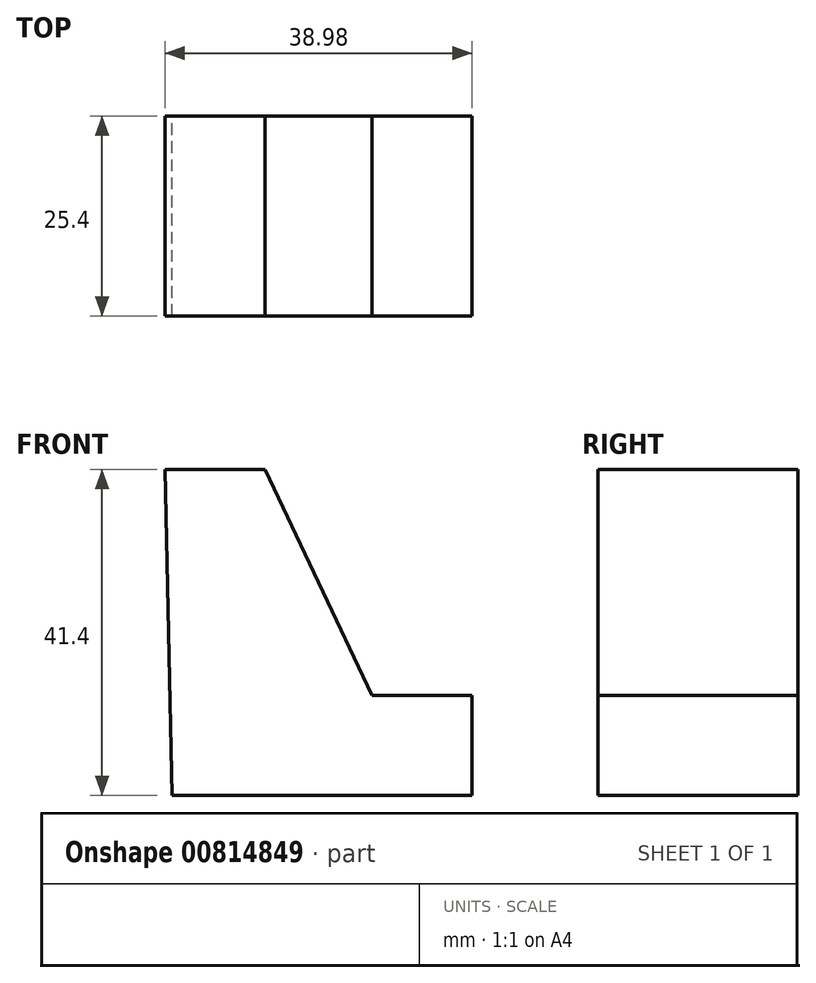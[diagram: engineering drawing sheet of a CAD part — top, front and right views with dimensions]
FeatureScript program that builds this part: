
annotation { "Feature Type Name" : "Feature", "Feature Type Description" : "" }
export const myFeature = defineFeature(function(context is Context, id is Id, definition is map)
    precondition{}
    {
        {
            var Q0;
            Q0=qCreatedBy(makeId("Front.planeOp"),FACE);
            var sketch = newSketch(context, id + "F0", { "sketchPlane" : qUnion([Q0])});
            skLineSegment(sketch, "E0", {"start": v(23.05, 0) * mm, "end": v(61.15, 0) * mm});
            skLineSegment(sketch, "E1", {"start": v(61.15, 0) * mm, "end": v(61.15, 12.7) * mm});
            skLineSegment(sketch, "E2", {"start": v(61.15, 12.7) * mm, "end": v(48.45, 12.7) * mm});
            skLineSegment(sketch, "E3", {"start": v(48.45, 12.7) * mm, "end": v(34.87, 41.4) * mm});
            skLineSegment(sketch, "E4", {"start": v(34.87, 41.4) * mm, "end": v(22.17, 41.4) * mm});
            skLineSegment(sketch, "E5", {"start": v(23.05, 0) * mm, "end": v(22.17, 41.4) * mm});
            skSolve(sketch);
        }
        {
            var Q0;
            Q0=makeQuery(id+"F0.imprint","IMPRINT",FACE,{"disambiguationData":[TD([[makeQuery(id+"F0.imprint","IMPRINT",EDGE,{"derivedFrom":sQuery(id+"F0.wireOp",EDGE,"E0")}),1.0]])]});
            extrude(context, id + "F1", {"entities" : qUnion([Q0]), "depth" : 25.4 * mm, "offsetDistance" : 25.4 * mm});
        }
    });
